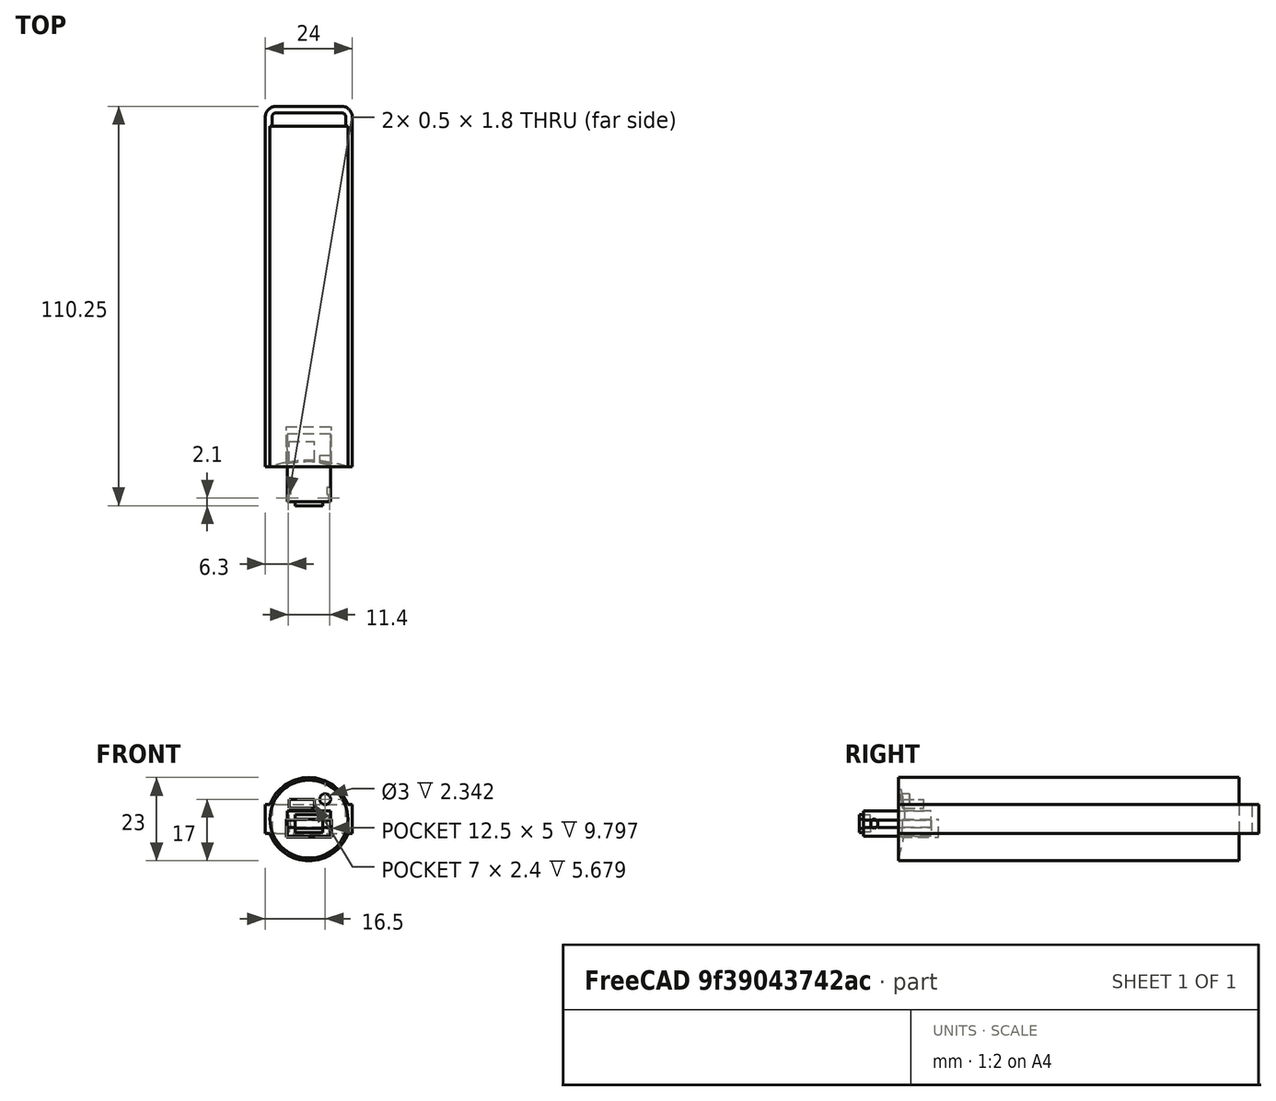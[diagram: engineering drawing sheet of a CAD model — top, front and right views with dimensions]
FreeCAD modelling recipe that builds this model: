
FCSTD DOCUMENT  (FreeCAD 0.19R)
Label: VARTA_Powerpack_Type_57959__3D
License: CreativeCommons Attribution-ShareAlike
LicenseURL: http://creativecommons.org/licenses/by-sa/4.0/
objects: Sketcher::SketchObject×10, PartDesign::Pad×5, TechDraw::DrawViewDimension×5, PartDesign::Pocket×4, TechDraw::DrawProjGroupItem×4, Part::Part2DObjectPython×2, PartDesign::Body×2, Part::Feature×2, PartDesign::Mirrored×2, PartDesign::SubtractiveSphere×1, App::Part×1, TechDraw::DrawSVGTemplate×1, TechDraw::DrawProjGroup×1, TechDraw::DrawPage×1, App::DocumentObjectGroup×1
note: 38 computed .brp shape members not serialized (recipe doc carries the construction recipe); baked Part::Feature solids carry a one-line shape summary decoded from their .brp

FEATURE [Sketcher::SketchObject] Sketch  label="BaseContur"
  MapMode = 5
  Placement = pos=(0,0,0) rot=(1,0,0;1.5708rad)
  Support = -> [XZ_Plane001]
  sketch-geometry (1):
    g0: Circle CenterX=0 CenterY=0 CenterZ=0 NormalX=0 NormalY=0 NormalZ=1 AngleXU=0 Radius=11.5
  constraints (2):
    c: Coincident(g0,g-1)
    c: Diameter(g0) = 23  'BaseDiameter'
FEATURE [PartDesign::Pad] Pad  label="BasePad"
  Length = 94
  Length2 = 100
  Placement = pos=(0,0,0) rot=(1,0,0;1.5708rad)
  Profile = -> Sketch
  Reversed = true
  Type = 0
FEATURE [Sketcher::SketchObject] Sketch001  label="BorderSketch"
  MapMode = 5
  Support = -> [XY_Plane001]
  sketch-geometry (18):
    g0: LineSegment StartX=-12 StartY=0 StartZ=0 EndX=-12 EndY=94 EndZ=0
    g1: LineSegment StartX=-12 StartY=94 StartZ=0 EndX=-12 EndY=96.5 EndZ=0
    g2: ArcOfCircle CenterX=-9 CenterY=96.5 CenterZ=0 NormalX=0 NormalY=0 NormalZ=1 AngleXU=0 Radius=3 StartAngle=1.5708 EndAngle=3.14159
    g3: LineSegment StartX=-9 StartY=99.5 StartZ=0 EndX=9 EndY=99.5 EndZ=0
    g4: ArcOfCircle CenterX=9 CenterY=96.5 CenterZ=0 NormalX=0 NormalY=0 NormalZ=1 AngleXU=0 Radius=3 StartAngle=0 EndAngle=1.5708
    g5: LineSegment StartX=12 StartY=96.5 StartZ=0 EndX=12 EndY=94 EndZ=0
    g6: LineSegment StartX=12 StartY=94 StartZ=0 EndX=12 EndY=0 EndZ=0
    g7: LineSegment [constr] StartX=-12 StartY=0 StartZ=0 EndX=12 EndY=0 EndZ=0
    g8: LineSegment StartX=-10.2 StartY=0 StartZ=0 EndX=-10.2 EndY=96.5 EndZ=0
    g9: ArcOfCircle CenterX=-9 CenterY=96.5 CenterZ=0 NormalX=0 NormalY=0 NormalZ=1 AngleXU=0 Radius=1.2 StartAngle=1.5708 EndAngle=3.14159
    g10: LineSegment StartX=-9 StartY=97.7 StartZ=0 EndX=9 EndY=97.7 EndZ=0
    g11: ArcOfCircle CenterX=9 CenterY=96.5 CenterZ=0 NormalX=0 NormalY=0 NormalZ=1 AngleXU=0 Radius=1.2 StartAngle=4.8e-15 EndAngle=1.5708
    g12: LineSegment StartX=10.2 StartY=96.5 StartZ=0 EndX=10.2 EndY=0 EndZ=0
    g13: LineSegment [constr] StartX=-12 StartY=96.5 StartZ=0 EndX=-10.2 EndY=96.5 EndZ=0
    g14: LineSegment [constr] StartX=12 StartY=96.5 StartZ=0 EndX=10.2 EndY=96.5 EndZ=0
    g15: LineSegment [constr] StartX=9 StartY=99.5 StartZ=0 EndX=9 EndY=97.7 EndZ=0
    g16: LineSegment StartX=-12 StartY=0 StartZ=0 EndX=-10.2 EndY=0 EndZ=0
    g17: LineSegment StartX=10.2 StartY=0 StartZ=0 EndX=12 EndY=0 EndZ=0
  constraints (45):
    c: PointOnObject(g0,g-1)
    c: Vertical(g0)
    c: Coincident(g0,g1)
    c: Tangent(g1,g2) = 1.5708
    c: Tangent(g2,g3) = 1.5708
    c: Tangent(g3,g4) = 1.5708
    c: Tangent(g4,g5) = 1.5708
    c: Coincident(g5,g6)
    c: Vertical(g6)
    c: Horizontal(g3)
    c: Equal(g4,g2)
    c: Vertical(g1)
    c: Equal(g1,g5)
    c: Equal(g6,g0)
    c: DistanceY(g0,g0) = 94  'BaseLength'
    c: DistanceY(g0,g2) = 5.5  'OverhangLength'
    c: DistanceX(g1,g4) = 24
    c: DistanceX(g1,g2) = 3
    c: Coincident(g7,g0)
    c: Coincident(g7,g6)
    c: Symmetric(g7,g7,g-1)
    c: PointOnObject(g8,g7)
    c: Vertical(g8)
    c: Tangent(g8,g9) = 1.5708
    c: Tangent(g9,g10) = 1.5708
    c: Tangent(g10,g11) = 1.5708
    c: Tangent(g11,g12) = 1.5708
    c: PointOnObject(g12,g7)
    c: Horizontal(g10)
    c: Coincident(g13,g1)
    c: Coincident(g13,g8)
    c: Horizontal(g14)
    c: Vertical(g12)
    c: Coincident(g11,g14)
    c: Equal(g14,g13)
    c: Horizontal(g13)
    c: DistanceX(g13,g13) = 1.8
    c: Coincident(g14,g4)
    c: Coincident(g15,g3)
    c: Coincident(g15,g10)
    c: Vertical(g15)
    c: Coincident(g16,g0)
    c: Coincident(g16,g8)
    c: Coincident(g17,g12)
    c: Coincident(g17,g6)
FEATURE [PartDesign::Pad] Pad001  label="BorderPad"
  BaseFeature = -> Pad
  Length = 8
  Length2 = 100
  Midplane = true
  Placement = pos=(0,0,0) rot=(1,0,0;1.5708rad)
  Profile = -> Sketch001
  Refine = true
  Type = 0
FEATURE [Sketcher::SketchObject] Sketch002  label="USB_OUTPUT_Sketch"
  MapMode = 5
  Placement = pos=(0,0,0) rot=(1,0,0;1.5708rad)
  Support = -> [XZ_Plane001]
  sketch-geometry (4):
    g0: LineSegment StartX=-6.25 StartY=0 StartZ=0 EndX=6.25 EndY=0 EndZ=0
    g1: LineSegment StartX=6.25 StartY=0 StartZ=0 EndX=6.25 EndY=-5 EndZ=0
    g2: LineSegment StartX=6.25 StartY=-5 StartZ=0 EndX=-6.25 EndY=-5 EndZ=0
    g3: LineSegment StartX=-6.25 StartY=-5 StartZ=0 EndX=-6.25 EndY=0 EndZ=0
  constraints (11):
    c: Coincident(g0,g1)
    c: Coincident(g1,g2)
    c: Coincident(g2,g3)
    c: Coincident(g3,g0)
    c: Horizontal(g0)
    c: Horizontal(g2)
    c: Vertical(g1)
    c: Vertical(g3)
    c: DistanceX(g2,g2) = 12.5
    c: DistanceY(g1,g1) = 5
    c: Symmetric(g0,g0,g-1)
FEATURE [Sketcher::SketchObject] Sketch003  label="USB_IN_Sketch"
  ExternalGeometry = -> [Pad001]
  MapMode = 5
  Placement = pos=(0,0,0) rot=(1,0,0;1.5708rad)
  Support = -> [XZ_Plane001]
  sketch-geometry (5):
    g0: LineSegment StartX=-5.5 StartY=5.4 StartZ=0 EndX=1.5 EndY=5.4 EndZ=0
    g1: LineSegment StartX=1.5 StartY=5.4 StartZ=0 EndX=1.5 EndY=3 EndZ=0
    g2: LineSegment StartX=1.5 StartY=3 StartZ=0 EndX=-5.5 EndY=3 EndZ=0
    g3: LineSegment StartX=-5.5 StartY=3 StartZ=0 EndX=-5.5 EndY=5.4 EndZ=0
    g4: LineSegment [constr] StartX=-2 StartY=4.2 StartZ=0 EndX=-2 EndY=0 EndZ=0
  constraints (17):
    c: Coincident(g0,g1)
    c: Coincident(g1,g2)
    c: Coincident(g2,g3)
    c: Coincident(g3,g0)
    c: Horizontal(g0)
    c: Horizontal(g2)
    c: Vertical(g1)
    c: Vertical(g3)
    c: DistanceY(g1,g1) = 2.4
    c: DistanceX(g0,g0) = 7
    c: DistanceX(g-3,g2) = 6.5
    c: PointOnObject(g4,g-1)
    c: Vertical(g4)
    c: Symmetric(g2,g0,g4)
    c: DistanceY(g-1,g1) = 3
    c: DistanceX(g4,g-1) = 2
    c: DistanceY(g4,g4) = 4.2
FEATURE [Sketcher::SketchObject] Sketch004  label="INFO_LED_Sketch"
  ExternalGeometry = -> [Pad001,Sketch003]
  MapMode = 5
  Placement = pos=(0,0,0) rot=(1,0,0;1.5708rad)
  Support = -> [XZ_Plane001]
  sketch-geometry (3):
    g0: Circle CenterX=4.5 CenterY=5.5 CenterZ=0 NormalX=0 NormalY=0 NormalZ=1 AngleXU=0 Radius=1.5
    g1: LineSegment [constr] StartX=7.28223 StartY=8.90051 StartZ=0 EndX=5.44986 EndY=6.66094 EndZ=0
    g2: LineSegment [constr] StartX=1.5 StartY=5.4 StartZ=0 EndX=3.00083 EndY=5.45003 EndZ=0
  constraints (12):
    c: Diameter(g0) = 3
    c: DistanceY(g-1,g0) = 5.5
    c: DistanceX(g-1,g0) = 4.5
    c: PointOnObject(g1,g-3)
    c: Perpendicular(g0,g1)
    c: PointOnObject(g1,g0)
    c: Perpendicular(g-3,g1)
    c: Distance(g1) = 2.89366
    c: Coincident(g2,g-4)
    c: PointOnObject(g2,g0)
    c: Perpendicular(g0,g2)
    c: Distance(g2) = 1.50167
FEATURE [Part::Part2DObjectPython] ShapeString  label="Label_IN"  # Draft 2D object (typed FeaturePython)
  FontFile = <userpath>/mydata/vision/webfonts/campivisivi.net_titillium/webfontkit-20120618-090220/titillium-boldupright-webfont.woff
  Placement = pos=(-3,0,6) rot=(1,0,0;1.5708rad)
  Size = 2
  String = IN
  Tracking = 0
FEATURE [Part::Part2DObjectPython] ShapeString001  label="Label_OUT"  # Draft 2D object (typed FeaturePython)
  FontFile = <userpath>/mydata/vision/webfonts/campivisivi.net_titillium/webfontkit-20120618-090220/titillium-boldupright-webfont.woff
  Placement = pos=(-2,0,-8) rot=(1,0,0;1.5708rad)
  Size = 2
  String = OUT
  Tracking = 0
FEATURE [PartDesign::SubtractiveSphere] Sphere
  Angle1 = -90
  Angle2 = 90
  Angle3 = 360
  AttacherType = Attacher::AttachEngine3D
  AttachmentOffset = pos=(0,0,31.2) rot=(-0.280175,0.959035,0.041872;0.309183rad)
  BaseFeature = -> Pad001
  MapMode = 2
  Placement = pos=(0,-31.2,6.9e-15) rot=(0.976395,0.145923,0.159247;1.50735rad)
  Radius = 33
  Refine = true
  Support = -> [Pad001]
FEATURE [PartDesign::Pocket] Pocket  label="INFO_LED_Pocket"
  BaseFeature = -> Sphere
  Length = 3
  Length2 = 100
  Placement = pos=(0,-31.2,7e-15) rot=(0.976395,0.145923,0.159247;1.50735rad)
  Profile = -> Sketch004
  Type = 0
FEATURE [PartDesign::Pocket] Pocket001  label="USB_IN_Pocket"
  BaseFeature = -> Pocket
  Length = 7
  Length2 = 100
  Placement = pos=(0,-31.2,7e-15) rot=(0.976395,0.145923,0.159247;1.50735rad)
  Profile = -> Sketch003
  Type = 0
FEATURE [PartDesign::Pocket] Pocket002  label="USB_OUT_Pocket"
  BaseFeature = -> Pocket001
  Length = 11
  Length2 = 100
  Placement = pos=(0,-31.2,7e-15) rot=(0.976395,0.145923,0.159247;1.50735rad)
  Profile = -> Sketch002
  Refine = true
  Type = 0
FEATURE [Sketcher::SketchObject] Sketch005  label="SphereHelperSketch"
  MapMode = 5
  Support = -> [XY_Plane001]
  sketch-geometry (1):
    g0: LineSegment [constr] StartX=0 StartY=0 StartZ=0 EndX=0 EndY=1.5 EndZ=0
  constraints (3):
    c: Coincident(g0,g-1)
    c: Vertical(g0)
    c: DistanceY(g0,g0) = 1.5
FEATURE [PartDesign::Body] Body  label="VARTA_Powerpack_Type_57959"
  Group = -> [Sketch,Pad,Sketch001,Pad001,Sketch002,Sketch003,Sketch004,Sphere,Sketch005,Pocket,Pocket001,Pocket002]
  Origin = -> Origin001
  Tip = -> Pocket002
FEATURE [Part::Feature] Body001  label="VARTA_Powerpack_Type_57960"
  shape: bbox 38.67 x 111.6 x 39.55 mm, 29 faces (baked)
FEATURE [Sketcher::SketchObject] Sketch006  label="BaseSketch"
  MapMode = 5
  Support = -> [XY_Plane002]
  sketch-geometry (5):
    g0: LineSegment StartX=-6 StartY=9 StartZ=0 EndX=6 EndY=9 EndZ=0
    g1: LineSegment StartX=6 StartY=9 StartZ=0 EndX=6 EndY=-9.65 EndZ=0
    g2: LineSegment StartX=6 StartY=-9.65 StartZ=0 EndX=-6 EndY=-9.65 EndZ=0
    g3: LineSegment StartX=-6 StartY=-9.65 StartZ=0 EndX=-6 EndY=9 EndZ=0
    g4: LineSegment [constr] StartX=0 StartY=9 StartZ=0 EndX=0 EndY=0 EndZ=0
  constraints (14):
    c: Coincident(g0,g1)
    c: Coincident(g1,g2)
    c: Coincident(g2,g3)
    c: Coincident(g3,g0)
    c: Horizontal(g0)
    c: Horizontal(g2)
    c: Vertical(g1)
    c: Vertical(g3)
    c: DistanceX(g2,g2) = 12
    c: DistanceY(g1,g1) = 18.65
    c: Vertical(g4)
    c: Coincident(g4,g-1)
    c: Symmetric(g0,g0,g4)
    c: DistanceY(g4,g4) = 9
FEATURE [PartDesign::Pad] Pad002
  Length = 4.5
  Length2 = 100
  Midplane = true
  Profile = -> Sketch006
  Type = 0
FEATURE [Sketcher::SketchObject] Sketch007
  MapMode = 5
  Placement = pos=(0,-9.65,0) rot=(1,0,0;1.5708rad)
  Support = -> [Pad002]
  expr: Constraints[10] = 4.5 / 2 + 1.45
  sketch-geometry (4):
    g0: LineSegment StartX=-3.8 StartY=0 StartZ=0 EndX=3.8 EndY=0 EndZ=0
    g1: LineSegment StartX=3.8 StartY=0 StartZ=0 EndX=3.8 EndY=-3.7 EndZ=0
    g2: LineSegment StartX=3.8 StartY=-3.7 StartZ=0 EndX=-3.8 EndY=-3.7 EndZ=0
    g3: LineSegment StartX=-3.8 StartY=-3.7 StartZ=0 EndX=-3.8 EndY=0 EndZ=0
  constraints (11):
    c: Coincident(g0,g1)
    c: Coincident(g1,g2)
    c: Coincident(g2,g3)
    c: Coincident(g3,g0)
    c: Horizontal(g0)
    c: Horizontal(g2)
    c: Vertical(g1)
    c: Vertical(g3)
    c: Symmetric(g0,g0,g-1)
    c: DistanceX(g2,g2) = 7.6
    c: DistanceY(g1,g1) = 3.7
FEATURE [PartDesign::Pad] Pad003
  BaseFeature = -> Pad002
  Length = 1.1
  Length2 = 100
  Profile = -> Sketch007
  Type = 0
FEATURE [Sketcher::SketchObject] Sketch008
  MapMode = 5
  Placement = pos=(0,0,-2.25) rot=(1,0,0;3.14159rad)
  Support = -> [Pad003]
  expr: Constraints[16] = 18.65 - 1 - 9
  expr: Constraints[15] = -4.5 / 2
  expr: Constraints[14] = -11.4 / 2
  sketch-geometry (6):
    g0: LineSegment StartX=-5.95 StartY=9.55 StartZ=0 EndX=-5.45 EndY=9.55 EndZ=0
    g1: LineSegment StartX=-5.45 StartY=9.55 StartZ=0 EndX=-5.45 EndY=7.75 EndZ=0
    g2: LineSegment StartX=-5.45 StartY=7.75 StartZ=0 EndX=-5.95 EndY=7.75 EndZ=0
    g3: LineSegment StartX=-5.95 StartY=7.75 StartZ=0 EndX=-5.95 EndY=9.55 EndZ=0
    g4: Circle [constr] CenterX=-2.25 CenterY=8.65 CenterZ=0 NormalX=0 NormalY=0 NormalZ=1 AngleXU=0 Radius=0.55
    g5: LineSegment [constr] StartX=-5.7 StartY=8.65 StartZ=0 EndX=-2.25 EndY=8.65 EndZ=0
  constraints (17):
    c: Coincident(g0,g1)
    c: Coincident(g1,g2)
    c: Coincident(g2,g3)
    c: Coincident(g3,g0)
    c: Horizontal(g0)
    c: Horizontal(g2)
    c: Vertical(g1)
    c: Vertical(g3)
    c: Diameter(g4) = 1.1
    c: Coincident(g5,g4)
    c: Symmetric(g2,g0,g5)
    c: Horizontal(g5)
    c: DistanceY(g3,g3) = 1.8
    c: DistanceX(g0,g0) = 0.5
    c: DistanceX(g5) = -5.7
    c: DistanceX(g4) = -2.25
    c: DistanceY(g4) = 8.65
FEATURE [PartDesign::Pad] Pad004
  BaseFeature = -> Pad003
  Length = 1.35
  Length2 = 100
  Profile = -> Sketch008
  Type = 0
FEATURE [PartDesign::Mirrored] Mirrored
  BaseFeature = -> Pad004
  MirrorPlane = -> Sketch008 [V_Axis]
  Originals = -> [Pad004]
FEATURE [Sketcher::SketchObject] Sketch009
  ExternalGeometry = -> [Mirrored]
  MapMode = 5
  Placement = pos=(6,0,0) rot=(0.57735,0.57735,0.57735;2.0944rad)
  Support = -> [Mirrored]
  sketch-geometry (5):
    g0: ArcOfCircle CenterX=-6.7 CenterY=-0.95 CenterZ=0 NormalX=0 NormalY=0 NormalZ=1 AngleXU=0 Radius=0.95 StartAngle=2e-16 EndAngle=3.14159
    g1: LineSegment StartX=-5.75 StartY=-0.95 StartZ=0 EndX=-5.75 EndY=-2.95 EndZ=0
    g2: LineSegment StartX=-5.75 StartY=-2.95 StartZ=0 EndX=-7.65 EndY=-2.95 EndZ=0
    g3: LineSegment StartX=-7.65 StartY=-2.95 StartZ=0 EndX=-7.65 EndY=-0.95 EndZ=0
    g4: LineSegment [constr] StartX=-6.7 StartY=0 StartZ=0 EndX=-6.7 EndY=-2.25 EndZ=0
  constraints (14):
    c: Coincident(g1,g2)
    c: Coincident(g2,g3)
    c: Horizontal(g2)
    c: Vertical(g1)
    c: Vertical(g3)
    c: Tangent(g0,g3) = 1.5708
    c: Tangent(g0,g1) = 1.5708
    c: DistanceX(g-3,g0) = 3.9
    c: DistanceX(g2,g2) = 1.9
    c: Vertical(g4)
    c: PointOnObject(g4,g-4)
    c: Perpendicular(g4,g0) = 4.71239
    c: PointOnObject(g4,g-1)
    c: DistanceY(g1,g1) = 2
FEATURE [PartDesign::Pocket] Pocket003
  BaseFeature = -> Mirrored
  Length = 1
  Length2 = 100
  Profile = -> Sketch009
  Type = 0
FEATURE [PartDesign::Mirrored] Mirrored001
  BaseFeature = -> Pocket003
  MirrorPlane = -> YZ_Plane002
  Originals = -> [Pocket003]
FEATURE [PartDesign::Body] Body002  label="lumberg_2410_08"
  Group = -> [Sketch006,Pad002,Sketch007,Pad003,Sketch008,Pad004,Mirrored,Sketch009,Pocket003,Mirrored001]
  Origin = -> Origin002
  Tip = -> Mirrored001
FEATURE [Part::Feature] Body002001  label="lumberg_2410_009"
  Placement = pos=(0,0,-2.5) rot=(0,1,0;3.14159rad)
  shape: bbox 12 x 19.75 x 5.95 mm, 30 faces (baked)
FEATURE [App::Part] Part  label="VARTA_Powerpack_Type_57959_Parts"
  Group = -> [Body,ShapeString,ShapeString001,Body001,Body002,Body002001]
  Origin = -> Origin
FEATURE [TechDraw::DrawSVGTemplate] Template
  EditableTexts = Designed_by_Name=Stefan Krüger; FC-Date=11.09.2019 14:32; FC-SC=1:100; FC-SH=1; FC-Title=VARTA Powerpack Type 57960; Subtitle=3d model to incorporate powerbank in other projects; drawing_name=basic usage; extra_information_value=https://github.com/<owner>/VARTA_Powerpack_Type_57959; version=0.1
  Height = 210
  Orientation = 1
  Width = 297
FEATURE [TechDraw::DrawProjGroupItem] ProjItem  label="Front"
  CoarseView = false
  Direction = (0,-1,0)
  Focus = 100
  HardHidden = false
  IsoCount = 0
  IsoHidden = false
  IsoVisible = false
  LockPosition = true
  Perspective = false
  Rotation = 0
  RotationVector = (1,0,0)
  ScaleType = 2
  SeamHidden = false
  SeamVisible = false
  SmoothHidden = false
  SmoothVisible = false
  Source = -> [Part]
  Type = 0
  X = 0
  Y = 0
FEATURE [TechDraw::DrawProjGroupItem] ProjItem001  label="Left"
  CoarseView = false
  Direction = (-1,-1e-16,0)
  Focus = 100
  HardHidden = false
  IsoCount = 0
  IsoHidden = false
  IsoVisible = false
  LockPosition = false
  Perspective = false
  Rotation = 0
  RotationVector = (1e-16,-1,0)
  ScaleType = 2
  SeamHidden = false
  SeamVisible = false
  SmoothHidden = false
  SmoothVisible = false
  Source = -> [Part]
  Type = 1
  X = 95.25
  Y = 0
FEATURE [TechDraw::DrawProjGroupItem] ProjItem002  label="FrontTopLeft"
  CoarseView = false
  Direction = (-1,-1,1)
  Focus = 100
  HardHidden = false
  IsoCount = 0
  IsoHidden = false
  IsoVisible = false
  LockPosition = false
  Perspective = false
  Rotation = 0
  RotationVector = (1,-1,0)
  ScaleType = 2
  SeamHidden = false
  SeamVisible = false
  SmoothHidden = false
  SmoothVisible = false
  Source = -> [Part]
  Type = 6
  X = 95.25
  Y = -75.25
FEATURE [TechDraw::DrawProjGroupItem] ProjItem003  label="Top"
  CoarseView = false
  Direction = (0,0,1)
  Focus = 100
  HardHidden = false
  IsoCount = 0
  IsoHidden = false
  IsoVisible = false
  LockPosition = false
  Perspective = false
  Rotation = 0
  RotationVector = (1,0,0)
  ScaleType = 2
  SeamHidden = false
  SeamVisible = false
  SmoothHidden = false
  SmoothVisible = false
  Source = -> [Part]
  Type = 4
  X = 0
  Y = -75.25
FEATURE [TechDraw::DrawProjGroup] ProjGroup
  Anchor = -> ProjItem
  AutoDistribute = true
  LockPosition = false
  ProjectionType = 0
  Rotation = 0
  ScaleType = 0
  Source = -> [Part]
  Views = -> [ProjItem,ProjItem001,ProjItem002,ProjItem003]
  X = 29.234
  Y = 177.156
  spacingX = -15
  spacingY = -35
FEATURE [TechDraw::DrawViewDimension] Dimension
  Arbitrary = false
  FormatSpec = %.3f
  LockPosition = false
  MeasureType = 1
  OverTolerance = 0
  References2D = -> [ProjItem001]
  Rotation = 0
  ScaleType = 0
  Type = 1
  UnderTolerance = 0
  X = 1.56073
  Y = -30.1755
FEATURE [TechDraw::DrawViewDimension] Dimension001
  Arbitrary = false
  FormatSpec = %.3f
  LockPosition = false
  MeasureType = 1
  OverTolerance = 0
  References2D = -> [ProjItem001]
  Rotation = 0
  ScaleType = 0
  Type = 2
  UnderTolerance = 0
  X = 65.6495
  Y = 2.5866
FEATURE [TechDraw::DrawViewDimension] Dimension002
  Arbitrary = false
  FormatSpec = %.3f
  LockPosition = false
  MeasureType = 1
  OverTolerance = 0
  References2D = -> [ProjItem001]
  Rotation = 0
  ScaleType = 0
  Type = 1
  UnderTolerance = 0
  X = 1.26251
  Y = -20.8169
FEATURE [TechDraw::DrawViewDimension] Dimension003
  Arbitrary = false
  FormatSpec = %.3f
  LockPosition = false
  MeasureType = 1
  OverTolerance = 0
  References2D = -> [ProjItem]
  Rotation = 0
  ScaleType = 0
  Type = 1
  UnderTolerance = 0
  X = 7.10472
  Y = -12.8451
FEATURE [TechDraw::DrawViewDimension] Dimension004
  Arbitrary = false
  FormatSpec = %.3f
  LockPosition = false
  MeasureType = 1
  OverTolerance = 0
  References2D = -> [ProjItem003]
  Rotation = 0
  ScaleType = 0
  Type = 2
  UnderTolerance = 0
  X = 31.2244
  Y = -34.3734
FEATURE [TechDraw::DrawPage] Page  label="Powerpack_Page"
  KeepUpdated = true
  NextBalloonIndex = 1
  ProjectionType = 0
  Template = -> Template
  Views = -> [ProjGroup,Dimension,Dimension001,Dimension002,Dimension003,Dimension004]
FEATURE [App::DocumentObjectGroup] Group  label="drawings"
  Group = -> [Page]
